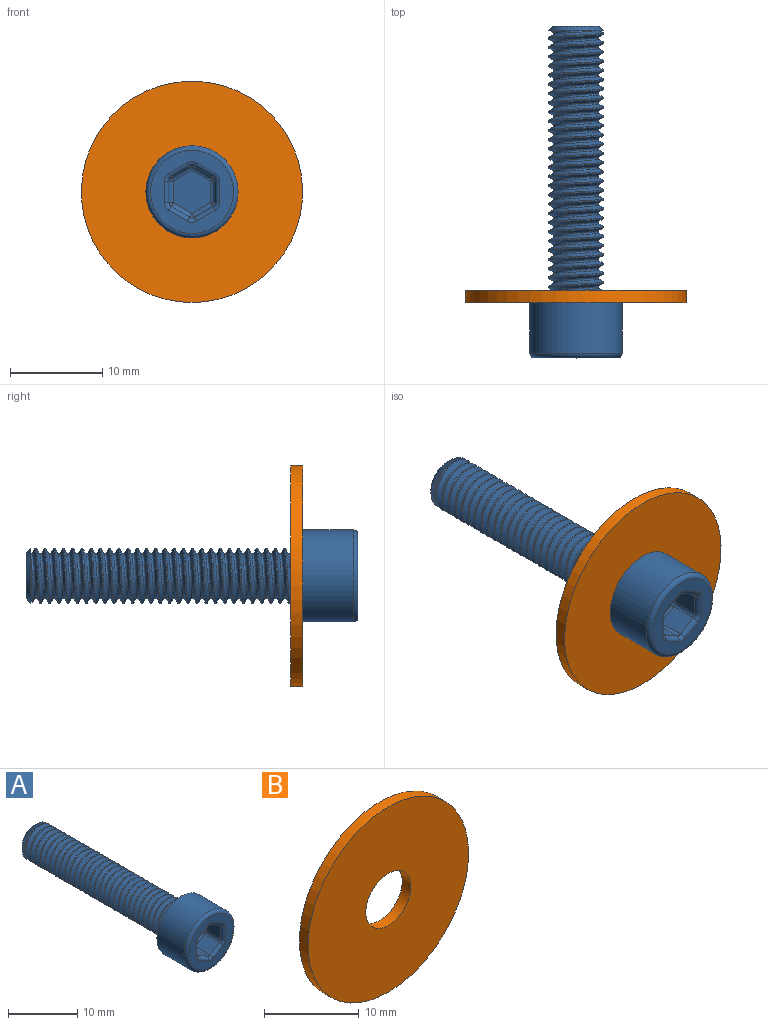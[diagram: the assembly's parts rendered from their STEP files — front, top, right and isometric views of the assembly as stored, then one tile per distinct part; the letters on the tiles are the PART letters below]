
ASSEMBLY  parts=2 mates=1
PART A: 51 faces, bbox 11.1x36.3x11.1 mm
  f0: cylinder r=3mm len=28.75mm, axis (0,-1,0), area 157mm2, adj f44,f46,f47,f50
  f1: plane 9x9mm, normal (0,-1,0), area 32.8mm2, adj f18,f22,f23,f27,f28,f33,f34,f37
  f2: plane 5x5mm, normal (0,1,0), area 19.6mm2, adj f3
  f3: cone r=2.5mm half-angle=45deg, axis (0,-1,0), area 12.2mm2, adj f2,f48
  f4: cylinder r=5mm len=10mm, axis (0,1,0), area 172.8mm2, adj f5,f43
  f5: plane 10x10mm, normal (0,1,0), area 40.1mm2, adj f4,f44
  f6: plane 3x2.31mm, normal (-1,0,0), area 6.9mm2, adj f31,f36,f39,f42
  f7: plane 3x2mm, normal (-0.5,0,-0.87), area 6.9mm2, adj f25,f26,f36,f37
  f8: plane 3x2mm, normal (0.5,0,-0.87), area 6.9mm2, adj f16,f17,f26,f27
  f9: plane 3x2.31mm, normal (1,0,0), area 6.9mm2, adj f13,f17,f18,f19
  f10: plane 3x2mm, normal (0.5,0,0.87), area 6.9mm2, adj f19,f20,f28,f29
  f11: plane 3x2mm, normal (-0.5,0,0.87), area 6.9mm2, adj f29,f30,f38,f39
  f12: plane 4.62x4mm, normal (0,-1,0), area 13.9mm2, adj f13,f16,f20,f25,f30,f31
  f13: cylinder r=0.5mm len=2.31mm, axis (0,0,1), area 1.8mm2, adj f9,f12,f14,f15
  f14: sphere r=0.5mm, area 0.2mm2, adj f13,f16,f17
  f15: sphere r=0.5mm, area 0.2mm2, adj f13,f19,f20
  f16: cylinder r=0.5mm len=2.25mm, axis (0.87,0,0.5), area 1.8mm2, adj f8,f12,f14,f21
  f17: cylinder r=0.5mm len=3mm, axis (0,-1,0), area 1.6mm2, adj f8,f9,f14,f22
  f18: cylinder r=0.5mm len=2.31mm, axis (0,0,1), area 1.8mm2, adj f1,f9,f22,f23
  f19: cylinder r=0.5mm len=3mm, axis (0,-1,0), area 1.6mm2, adj f9,f10,f15,f23
  f20: cylinder r=0.5mm len=2.25mm, axis (-0.87,0,0.5), area 1.8mm2, adj f10,f12,f15,f24
  f21: sphere r=0.5mm, area 0.3mm2, adj f16,f25,f26
  f22: torus R=1mm, axis (0,-1,0), area 0.6mm2, adj f1,f17,f18,f27
  f23: torus R=1mm, axis (0,-1,0), area 0.6mm2, adj f1,f18,f19,f28
  f24: sphere r=0.5mm, area 0.3mm2, adj f20,f29,f30
  f25: cylinder r=0.5mm len=2.25mm, axis (0.87,0,-0.5), area 1.8mm2, adj f7,f12,f21,f32
  f26: cylinder r=0.5mm len=3mm, axis (0,-1,0), area 1.6mm2, adj f7,f8,f21,f33
  f27: cylinder r=0.5mm len=2.25mm, axis (0.87,0,0.5), area 1.8mm2, adj f1,f8,f22,f33
  f28: cylinder r=0.5mm len=2.25mm, axis (-0.87,0,0.5), area 1.8mm2, adj f1,f10,f23,f34
  f29: cylinder r=0.5mm len=3mm, axis (0,-1,0), area 1.6mm2, adj f10,f11,f24,f34
  f30: cylinder r=0.5mm len=2.25mm, axis (-0.87,0,-0.5), area 1.8mm2, adj f11,f12,f24,f35
  f31: cylinder r=0.5mm len=2.31mm, axis (0,0,-1), area 1.8mm2, adj f6,f12,f32,f35
  f32: sphere r=0.5mm, area 0.2mm2, adj f25,f31,f36
  f33: torus R=1mm, axis (0,-1,0), area 0.6mm2, adj f1,f26,f27,f37
  f34: torus R=1mm, axis (0,-1,0), area 0.6mm2, adj f1,f28,f29,f38
  f35: sphere r=0.5mm, area 0.2mm2, adj f30,f31,f39
  f36: cylinder r=0.5mm len=3mm, axis (0,-1,0), area 1.6mm2, adj f6,f7,f32,f40
  f37: cylinder r=0.5mm len=2.25mm, axis (0.87,0,-0.5), area 1.8mm2, adj f1,f7,f33,f40
  f38: cylinder r=0.5mm len=2.25mm, axis (-0.87,0,-0.5), area 1.8mm2, adj f1,f11,f34,f41
  f39: cylinder r=0.5mm len=3mm, axis (0,-1,0), area 1.6mm2, adj f6,f11,f35,f41
  f40: torus R=1mm, axis (0,-1,0), area 0.6mm2, adj f1,f36,f37,f42
  f41: torus R=1mm, axis (0,-1,0), area 0.6mm2, adj f1,f38,f39,f42
  f42: cylinder r=0.5mm len=2.31mm, axis (0,0,-1), area 1.8mm2, adj f1,f6,f40,f41
  f43: torus R=4.5mm, axis (0,-1,0), area 23.8mm2, adj f1,f4
  f44: torus R=3.5mm, axis (0,-1,0), area 15.7mm2, adj f0,f5,f49
  f45: bspline ~29.75x5.68mm, area 123.1mm2, adj f46,f47,f48,f49
  f46: bspline ~29.81x6.93mm, area 309.8mm2, adj f0,f45,f48,f49,f50
  f47: bspline ~29.48x6.93mm, area 311.3mm2, adj f0,f45,f48,f49,f50
  f48: plane 6.03x6.03mm, normal (0,-1,0), area 9mm2, adj f3,f45,f46,f47,f50
  f49: plane 6.28x6.28mm, normal (0,1,0), area 5.5mm2, adj f44,f45,f46,f47
  f50: cone r=3mm half-angle=63.4deg, axis (0,-1,0), area 3.9mm2, adj f0,f46,f47,f48
PART B: 4 faces, bbox 24x1.3x24 mm
  f0: plane 24x24mm, normal (0,1,0), area 416.6mm2, adj f1,f2
  f1: cylinder r=3.38mm len=6.75mm, axis (0,-1,0), area 27.6mm2, adj f0,f3
  f2: cylinder r=12mm len=24mm, axis (0,-1,0), area 98mm2, adj f0,f3
  f3: plane 24x24mm, normal (0,-1,0), area 416.6mm2, adj f1,f2
PLACE A at identity
PLACE B at identity fixed
MATE fastened B.f1 <-> A.f4  axis (0,-1,0) through (0,0,0)mm
